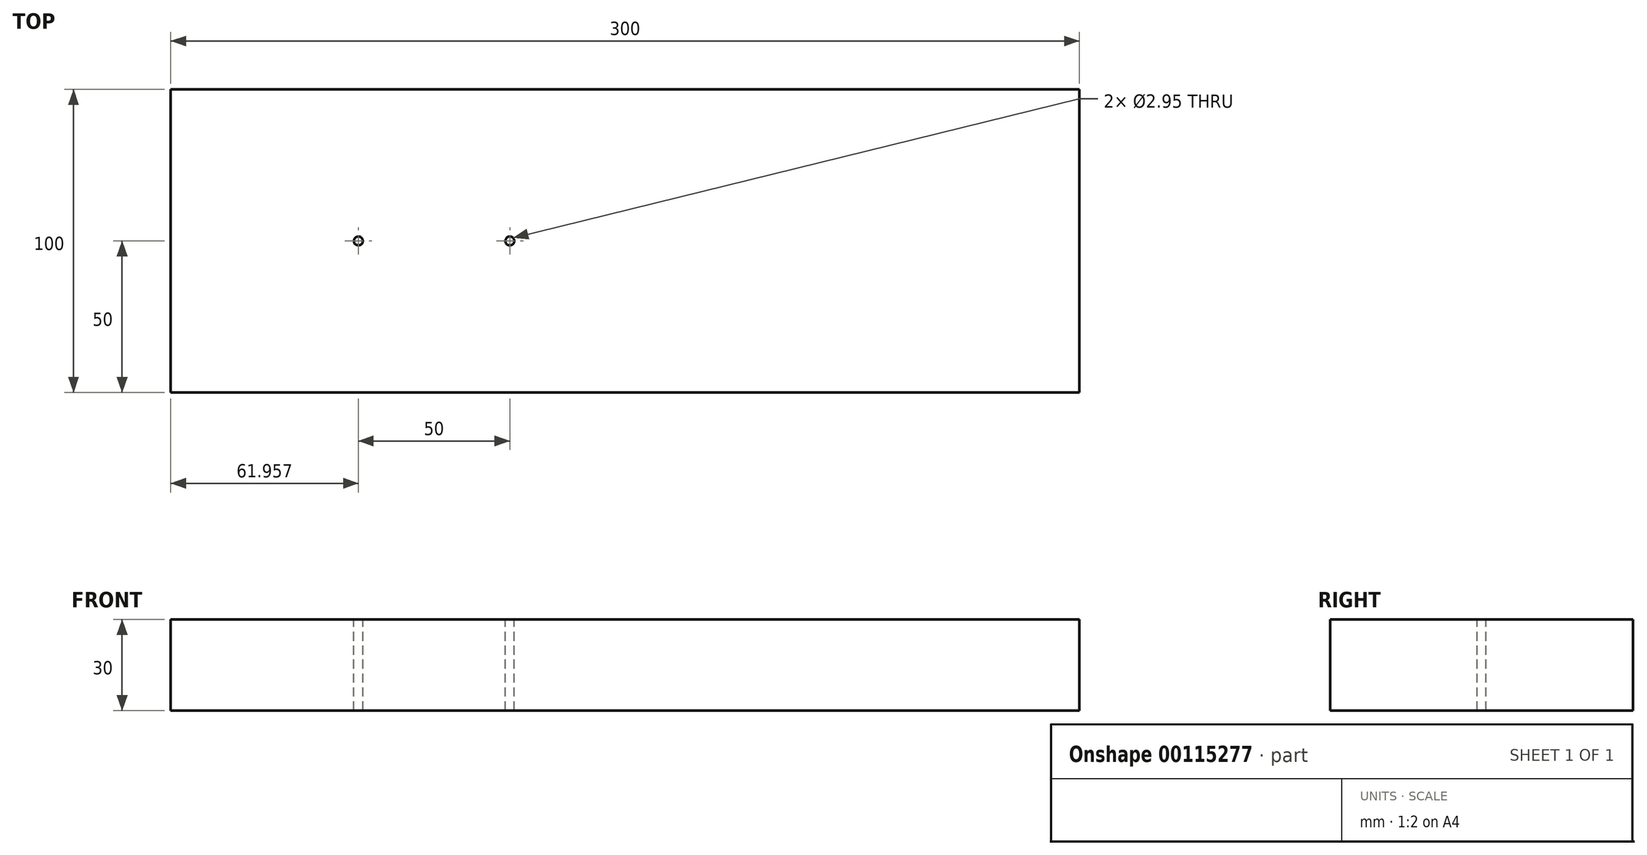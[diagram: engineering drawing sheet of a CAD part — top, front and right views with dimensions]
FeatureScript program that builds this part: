
annotation { "Feature Type Name" : "Feature", "Feature Type Description" : "" }
export const myFeature = defineFeature(function(context is Context, id is Id, definition is map)
    precondition{}
    {
        {
            var Q0;
            Q0=qCreatedBy(makeId("Top.planeOp"),FACE);
            var sketch = newSketch(context, id + "F0", { "sketchPlane" : qUnion([Q0])});
            skLineSegment(sketch, "E0.bottom", {"start": v(150, -50) * mm, "end": v(-150, -50) * mm});
            skLineSegment(sketch, "E0.top", {"start": v(150, 50) * mm, "end": v(-150, 50) * mm});
            skLineSegment(sketch, "E0.left", {"start": v(150, -50) * mm, "end": v(150, 50) * mm});
            skLineSegment(sketch, "E0.right", {"start": v(-150, -50) * mm, "end": v(-150, 50) * mm});
            skPoint(sketch, "E0.middle", {"position": v(0, 0) * mm});
            skSolve(sketch);
        }
        {
            var Q0;
            Q0=makeQuery(id+"F0.imprint","IMPRINT",FACE,{"disambiguationData":[TD([[makeQuery(id+"F0.imprint","IMPRINT",EDGE,{"derivedFrom":sQuery(id+"F0.wireOp",EDGE,"E0.bottom")}),-1.0]])]});
            extrude(context, id + "F1", {"entities" : qUnion([Q0]), "depth" : 30 * mm});
        }
        {
            var Q0;
            Q0=makeQuery(id+"F1.opExtrude","CAP_FACE",FACE,{"disambiguationData":[OSD([sQuery(id+"F0.wireOp",EDGE,"E0.bottom"),sQuery(id+"F0.wireOp",EDGE,"E0.top"),sQuery(id+"F0.wireOp",EDGE,"E0.left"),sQuery(id+"F0.wireOp",EDGE,"E0.right")])],"isStart":false});
            var sketch = newSketch(context, id + "F2", { "sketchPlane" : qUnion([Q0])});
            skCircle(sketch, "E1", {"center": v(-38.04, 0) * mm, "radius": 1.48 * mm});
            skCircle(sketch, "E2.1.0.0", {"center": v(-88.04, 0) * mm, "radius": 1.48 * mm});
            skLineSegment(sketch, "E2.direction1", {"start": v(-38.04, 0) * mm, "end": v(-88.04, 0) * mm, "construction": true});
            skSolve(sketch);
        }
        {
            var Q0;
            Q0 = qSketchRegion(id + "F2", true);
            var Q1;
            Q1=makeQuery(id+"F1.opExtrude","CAP_FACE",FACE,{"disambiguationData":[OSD([sQuery(id+"F0.wireOp",EDGE,"E0.bottom"),sQuery(id+"F0.wireOp",EDGE,"E0.top"),sQuery(id+"F0.wireOp",EDGE,"E0.left"),sQuery(id+"F0.wireOp",EDGE,"E0.right")])],"isStart":true});
            extrude(context, id + "F3", {"entities" : qUnion([Q0]), "operationType" : NewBodyOperationType.REMOVE, "endBound" : BoundingType.UP_TO_SURFACE, "oppositeDirection" : true, "endBoundEntityFace" : qUnion([Q1]), "depth" : 25 * mm});
        }
    });
